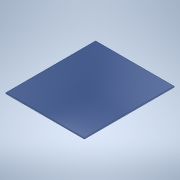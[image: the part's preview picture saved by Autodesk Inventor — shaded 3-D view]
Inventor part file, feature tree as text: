
AUTODESK INVENTOR PART (.ipt)
format: ipt  version: 2020 (Build 240168000, 168)  size: 97,792 bytes
history: native  units: in
note: dims shown in document units (in); Inventor stores cm internally (conversion verified against a paired STEP export)
features: extrude x1, sketch x1
ambient origin geometry x8: Origin, YZ Plane, XZ Plane, XY Plane, X Axis, Y Axis, Z Axis, Center Point
bodies: Solid1 (feature_tree)
feature tree (2):
  extrude  "Extrusion1"  Depth=16.0in
  sketch  "Sketch1"  dims[d0=14.0in d1=16.0in d2=0.1875in d3=0.0in]
